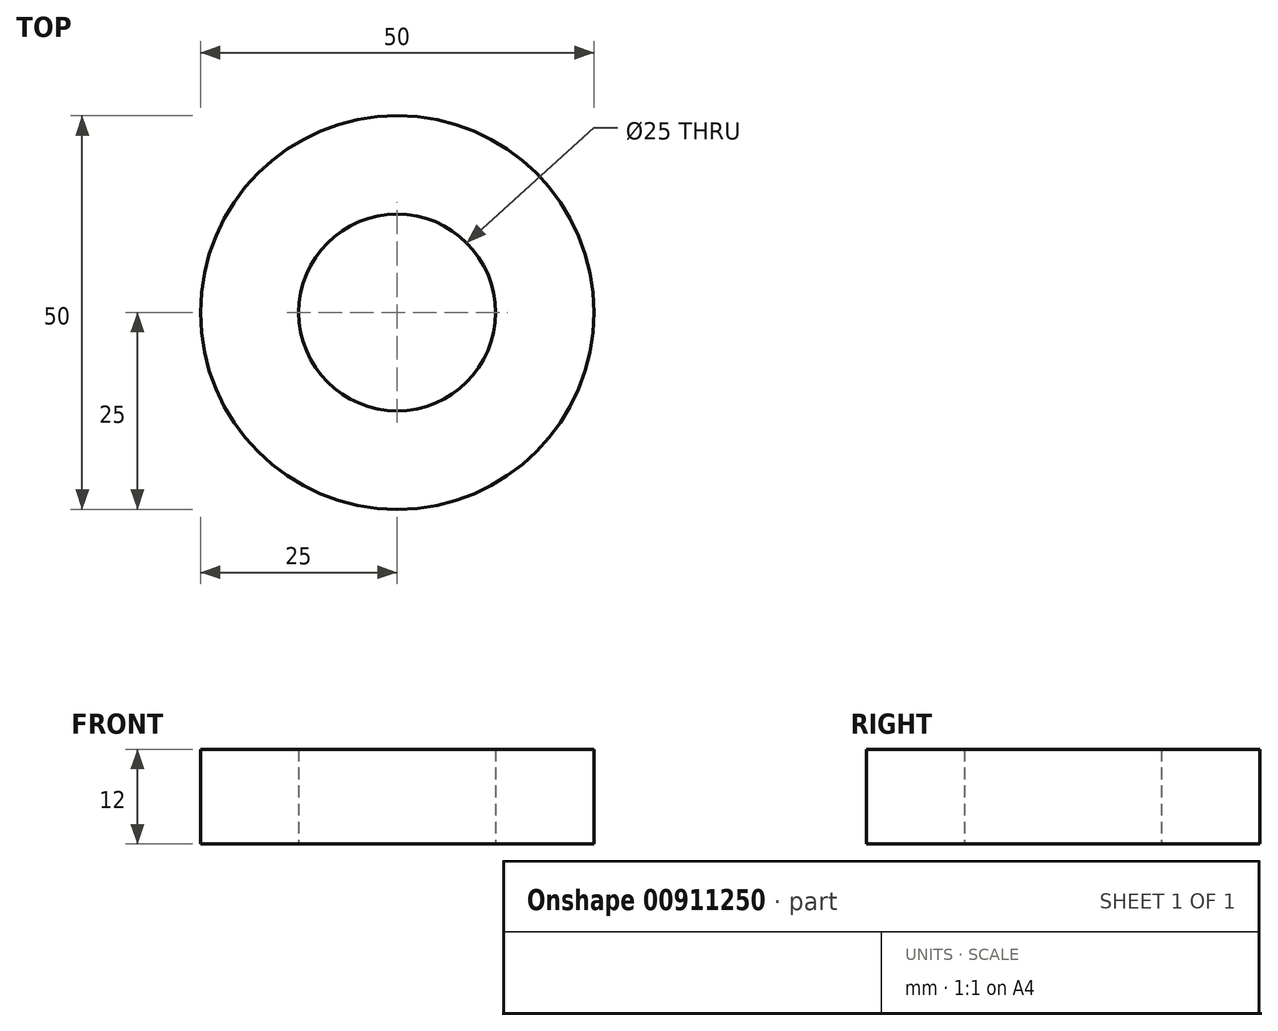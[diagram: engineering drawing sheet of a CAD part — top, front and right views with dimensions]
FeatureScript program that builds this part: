
annotation { "Feature Type Name" : "Feature", "Feature Type Description" : "" }
export const myFeature = defineFeature(function(context is Context, id is Id, definition is map)
    precondition{}
    {
        {
            var Q0;
            Q0=qCreatedBy(makeId("Top.planeOp"),FACE);
            var sketch = newSketch(context, id + "F0", { "sketchPlane" : qUnion([Q0])});
            skCircle(sketch, "E0", {"center": v(0, 0) * mm, "radius": 12.5 * mm});
            skCircle(sketch, "E1", {"center": v(0, 0) * mm, "radius": 25 * mm});
            skSolve(sketch);
        }
        {
            var Q0;
            Q0=makeQuery(id+"F0.imprint","IMPRINT",FACE,{"disambiguationData":[TD([[makeQuery(id+"F0.imprint","IMPRINT",EDGE,{"derivedFrom":sQuery(id+"F0.wireOp",EDGE,"E0")}),-1.0]])]});
            extrude(context, id + "F1", {"entities" : qUnion([Q0]), "depth" : 12 * mm, "offsetDistance" : 25 * mm});
        }
    });
